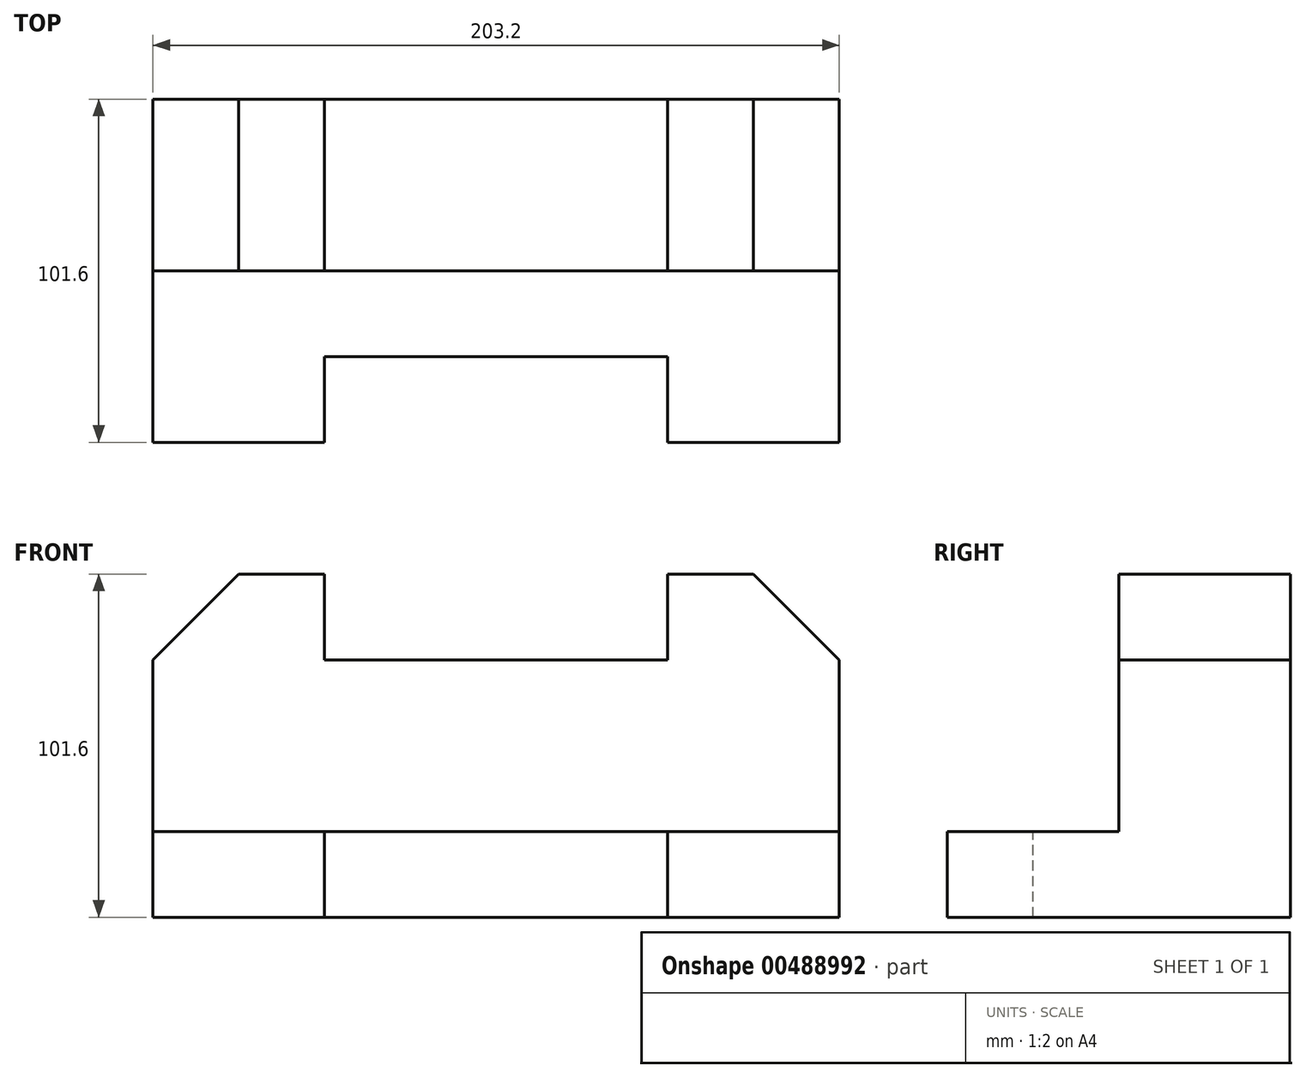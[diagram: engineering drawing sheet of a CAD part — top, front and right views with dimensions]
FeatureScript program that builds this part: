
annotation { "Feature Type Name" : "Feature", "Feature Type Description" : "" }
export const myFeature = defineFeature(function(context is Context, id is Id, definition is map)
    precondition{}
    {
        {
            var Q0;
            Q0=qCreatedBy(makeId("Top.planeOp"),FACE);
            var sketch = newSketch(context, id + "F0", { "sketchPlane" : qUnion([Q0])});
            skLineSegment(sketch, "E0.bottom", {"start": v(-92.18, 60) * mm, "end": v(111.02, 60) * mm});
            skLineSegment(sketch, "E0.top", {"start": v(-92.18, -41.6) * mm, "end": v(111.02, -41.6) * mm});
            skLineSegment(sketch, "E0.left", {"start": v(-92.18, 60) * mm, "end": v(-92.18, -41.6) * mm});
            skLineSegment(sketch, "E0.right", {"start": v(111.02, 60) * mm, "end": v(111.02, -41.6) * mm});
            skSolve(sketch);
        }
        {
            var Q0;
            Q0 = qSketchRegion(id + "F0", true);
            extrude(context, id + "F1", {"entities" : qUnion([Q0]), "depth" : 101.6 * mm});
        }
        {
            var Q0;
            Q0=makeQuery(id+"F1.opExtrude","SWEPT_FACE",FACE,{"disambiguationData":[OSD([sQuery(id+"F0.wireOp",EDGE,"E0.right")])]});
            var sketch = newSketch(context, id + "F2", { "sketchPlane" : qUnion([Q0])});
            skLineSegment(sketch, "E1.bottom", {"start": v(-41.6, 101.6) * mm, "end": v(9.2, 101.6) * mm});
            skLineSegment(sketch, "E1.top", {"start": v(-41.6, 25.4) * mm, "end": v(9.2, 25.4) * mm});
            skLineSegment(sketch, "E1.left", {"start": v(-41.6, 101.6) * mm, "end": v(-41.6, 25.4) * mm});
            skLineSegment(sketch, "E1.right", {"start": v(9.2, 101.6) * mm, "end": v(9.2, 25.4) * mm});
            skSolve(sketch);
        }
        {
            var Q0;
            Q0 = qSketchRegion(id + "F2", true);
            extrude(context, id + "F3", {"entities" : qUnion([Q0]), "operationType" : NewBodyOperationType.REMOVE, "endBound" : BoundingType.THROUGH_ALL, "oppositeDirection" : true, "depth" : 25.4 * mm});
        }
        {
            var Q0;
            Q0=makeQuery(id+"F3.boolean.opBoolean","COPY",FACE,{"derivedFrom":makeQuery(id+"F3.opExtrude","SWEPT_FACE",FACE,{"disambiguationData":[OSD([sQuery(id+"F2.wireOp",EDGE,"E1.top")])]})});
            var sketch = newSketch(context, id + "F4", { "sketchPlane" : qUnion([Q0])});
            skLineSegment(sketch, "E2.bottom", {"start": v(-41.38, -41.6) * mm, "end": v(60.22, -41.6) * mm});
            skLineSegment(sketch, "E2.top", {"start": v(-41.38, -16.2) * mm, "end": v(60.22, -16.2) * mm});
            skLineSegment(sketch, "E2.left", {"start": v(-41.38, -41.6) * mm, "end": v(-41.38, -16.2) * mm});
            skLineSegment(sketch, "E2.right", {"start": v(60.22, -41.6) * mm, "end": v(60.22, -16.2) * mm});
            skSolve(sketch);
        }
        {
            var Q0;
            Q0 = qSketchRegion(id + "F4", true);
            extrude(context, id + "F5", {"entities" : qUnion([Q0]), "operationType" : NewBodyOperationType.REMOVE, "endBound" : BoundingType.THROUGH_ALL, "oppositeDirection" : true, "depth" : 25.4 * mm});
        }
        {
            var Q0;
            Q0=makeQuery(id+"F3.boolean.opBoolean","COPY",FACE,{"derivedFrom":makeQuery(id+"F3.opExtrude","SWEPT_FACE",FACE,{"disambiguationData":[OSD([sQuery(id+"F2.wireOp",EDGE,"E1.right")])]})});
            var sketch = newSketch(context, id + "F6", { "sketchPlane" : qUnion([Q0])});
            skLineSegment(sketch, "E3.bottom", {"start": v(-41.38, 101.6) * mm, "end": v(60.22, 101.6) * mm});
            skLineSegment(sketch, "E3.top", {"start": v(-41.38, 76.2) * mm, "end": v(60.22, 76.2) * mm});
            skLineSegment(sketch, "E3.left", {"start": v(-41.38, 101.6) * mm, "end": v(-41.38, 76.2) * mm});
            skLineSegment(sketch, "E3.right", {"start": v(60.22, 101.6) * mm, "end": v(60.22, 76.2) * mm});
            skSolve(sketch);
        }
        {
            var Q0;
            Q0 = qSketchRegion(id + "F6", true);
            extrude(context, id + "F7", {"entities" : qUnion([Q0]), "operationType" : NewBodyOperationType.REMOVE, "endBound" : BoundingType.THROUGH_ALL, "oppositeDirection" : true, "depth" : 25.4 * mm});
        }
        {
            var Q0;
            Q0=makeQuery(id+"F3.boolean.opBoolean","COPY",FACE,{"derivedFrom":makeQuery(id+"F3.opExtrude","SWEPT_FACE",FACE,{"disambiguationData":[OSD([sQuery(id+"F2.wireOp",EDGE,"E1.right")])]})});
            var sketch = newSketch(context, id + "F8", { "sketchPlane" : qUnion([Q0])});
            skLineSegment(sketch, "E4", {"start": v(85.62, 101.6) * mm, "end": v(111.02, 76.2) * mm});
            skLineSegment(sketch, "E5", {"start": v(-66.78, 101.6) * mm, "end": v(-92.18, 76.2) * mm});
            skSolve(sketch);
        }
        {
            var Q0;
            {var subQ0=sQuery(id+"F8.wireOp",EDGE,"E5");Q0=makeQuery(id+"F8.imprint","IMPRINT",FACE,{"disambiguationData":[TD([[makeQuery(id+"F8.imprint","IMPRINT",EDGE,{"derivedFrom":subQ0}),-1.0]])]});}
            var Q1;
            {var subQ0=sQuery(id+"F8.wireOp",EDGE,"E4");Q1=makeQuery(id+"F8.imprint","IMPRINT",FACE,{"disambiguationData":[TD([[makeQuery(id+"F8.imprint","IMPRINT",EDGE,{"derivedFrom":subQ0}),1.0]])]});}
            extrude(context, id + "F9", {"entities" : qUnion([Q0, Q1]), "operationType" : NewBodyOperationType.REMOVE, "endBound" : BoundingType.THROUGH_ALL, "oppositeDirection" : true, "depth" : 25.4 * mm});
        }
    });
